# Revit family: CONV_Pholc_GnrlPrpseLmnrs_Mobil150Wall
name_source: partatom
category: Lighting Fixtures
revit_build: Autodesk Revit 2015 (Build: 20140606_1530(x64)
units: mm (PartAtom-declared; Revit-internal decimal feet)

## types (1)
- Black
    Apparent Load = 0 VA
    ArticleNumber = 511215
    AssetType = Fixed
    BIMObjectName = CONV_Pholc_GnrlPrpseLmnrs_Mobil150Wall
    Brand = Pholc
    BulbIncluded = No
    Category = Wall lamps
    Collection = Soft Reflections
    Color = Black
    Color Filter = 16777215
    ConvergoRefNr = 0103-1704-0004-SE
    Default Elevation = 0 mm  [stored 0 ft]
    Designer = Monika Mulder
    Dimmer = Yes
    Dimming Lamp Color Temperature Shift = <None>
    DurationUnit = Year
    ElectricalDeviceNominalPower = 0
    ExpiringDate = 12/2017
    Finish = Lacquered
    HasProtectiveEarth = No
    IfcExportAs = IfcLightFixtureType
    IfcExportType = NOTDEFINED
    LensMaterial = Glass, Frosted
    Light Source Symbol Size = 150 mm
    LightFixtureMainMaterial = Steel black
    LightFixtureSecondaryMaterial = Black Textile
    MaintenanceFactor = 0
    ManufacterURL = www.pholc.se
    Manufacturer = Pholc
    ManufacturerName = Pholc
    Material = Steel
    MaxWatt = 20 W
    Model = Mobil 150 Wall
    ModelNumber = 511215
    NBSDescription = General purpose luminaires
    NBSReference = 90-60-50/405
    Name = GnrlPrpseLmnrs_Mobil150Wall
    NominalCurrent = 0 A
    NominalDepth = 167 mm  [stored 0.5479 ft]
    NominalFrequencyRange = 0 Hz
    NominalHeight = 1500 mm  [stored 4.92126 ft]
    NominalVoltage = 0 V
    NominalVoltageCalc = 0 V
    NominalWidth = 140 mm  [stored 0.459318 ft]
    NumberOfPoles = 1
    NumberOfSources = 0
    On/OffSwitch = Yes
    PhaseAngle = 0.00°
    Shape = Sculptured
    Size = 140x167x1500mm
    Socket = G9 Base
    TotalWattage = 0 W
    URL = http://www.pholc.se
    Uniclass2 = Pr_70_70_49_86
    Uniclass2015Description = Suspended luminaires
    Uniclass2015Reference = Pr_70_70_48_86
    UsageCurrent = 0 A
    Version = 1
    VersionDate = 04/04/2017
    WarrantyDurationUnit = Year

note: [stored X ft] marks values corroborated as IEEE doubles in the binary element streams (Revit-internal decimal feet)

## geometry (parser evidence)
native form markers: Sweep x2
no freeform markers — native parametric forms only
